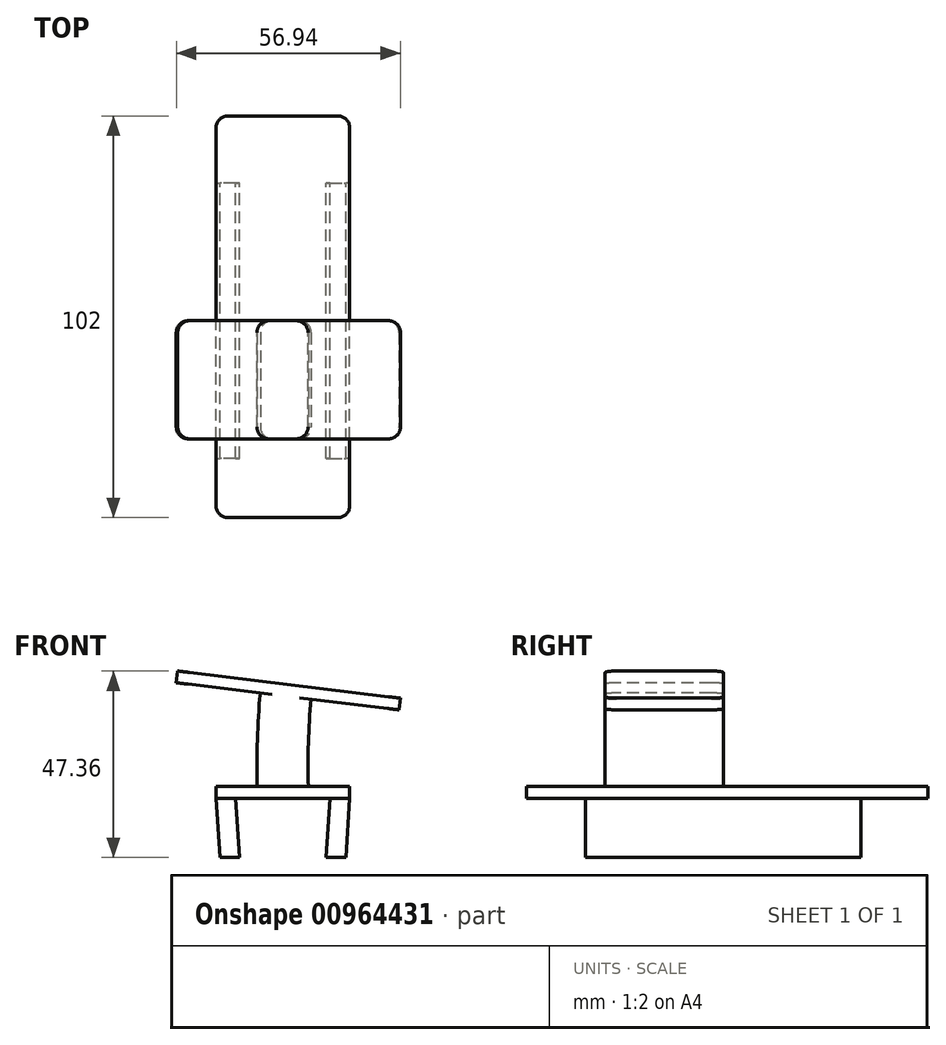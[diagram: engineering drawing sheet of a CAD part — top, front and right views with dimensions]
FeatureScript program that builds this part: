
annotation { "Feature Type Name" : "Feature", "Feature Type Description" : "" }
export const myFeature = defineFeature(function(context is Context, id is Id, definition is map)
    precondition{}
    {
        {
            var Q0;
            Q0=qCreatedBy(makeId("Top.planeOp"),FACE);
            var sketch = newSketch(context, id + "F0", { "sketchPlane" : qUnion([Q0])});
            skLineSegment(sketch, "E0.bottom", {"start": v(-17, -50) * mm, "end": v(17, -50) * mm});
            skLineSegment(sketch, "E0.top", {"start": v(-17, 52) * mm, "end": v(17, 52) * mm});
            skLineSegment(sketch, "E0.left", {"start": v(-17, -50) * mm, "end": v(-17, 52) * mm});
            skLineSegment(sketch, "E0.right", {"start": v(17, -50) * mm, "end": v(17, 52) * mm});
            skSolve(sketch);
        }
        {
            var Q0;
            Q0=makeQuery(id+"F0.imprint","IMPRINT",FACE,{"disambiguationData":[TD([[makeQuery(id+"F0.imprint","IMPRINT",EDGE,{"derivedFrom":sQuery(id+"F0.wireOp",EDGE,"E0.bottom")}),1.0]])]});
            extrude(context, id + "F1", {"entities" : qUnion([Q0]), "depth" : 3 * mm, "offsetDistance" : 25 * mm});
        }
        {
            var Q0;
            Q0=makeQuery(id+"F1.opExtrude","CAP_FACE",FACE,{"disambiguationData":[OSD([sQuery(id+"F0.wireOp",EDGE,"E0.bottom"),sQuery(id+"F0.wireOp",EDGE,"E0.top"),sQuery(id+"F0.wireOp",EDGE,"E0.left"),sQuery(id+"F0.wireOp",EDGE,"E0.right")])],"isStart":true});
            var sketch = newSketch(context, id + "F2", { "sketchPlane" : qUnion([Q0])});
            skLineSegment(sketch, "E1.bottom", {"start": v(12, 35) * mm, "end": v(17, 35) * mm});
            skLineSegment(sketch, "E1.top", {"start": v(12, -35) * mm, "end": v(17, -35) * mm});
            skLineSegment(sketch, "E1.left", {"start": v(12, 35) * mm, "end": v(12, -35) * mm});
            skLineSegment(sketch, "E1.right", {"start": v(17, 35) * mm, "end": v(17, -35) * mm});
            skLineSegment(sketch, "E2.MirrorCS", {"start": v(-12, 35) * mm, "end": v(-17, 35) * mm});
            skLineSegment(sketch, "E3.MirrorCS", {"start": v(-12, 35) * mm, "end": v(-12, -35) * mm});
            skLineSegment(sketch, "E4.MirrorCS", {"start": v(-17, 35) * mm, "end": v(-17, -35) * mm});
            skLineSegment(sketch, "E5.MirrorCS", {"start": v(-12, -35) * mm, "end": v(-17, -35) * mm});
            skSolve(sketch);
        }
        {
            var Q0;
            Q0=makeQuery(id+"F1.opExtrude","CAP_FACE",FACE,{"disambiguationData":[OSD([sQuery(id+"F0.wireOp",EDGE,"E0.bottom"),sQuery(id+"F0.wireOp",EDGE,"E0.top"),sQuery(id+"F0.wireOp",EDGE,"E0.left"),sQuery(id+"F0.wireOp",EDGE,"E0.right")])],"isStart":false});
            var sketch = newSketch(context, id + "F3", { "sketchPlane" : qUnion([Q0])});
            skLineSegment(sketch, "E6", {"start": v(0, 0) * mm, "end": v(-6.5, 0) * mm});
            skLineSegment(sketch, "E7", {"start": v(-6.5, 0) * mm, "end": v(-6.5, -30) * mm});
            skLineSegment(sketch, "E8", {"start": v(-6.5, -30) * mm, "end": v(0, -30) * mm});
            skLineSegment(sketch, "E9.MirrorCS", {"start": v(0, 0) * mm, "end": v(6.5, 0) * mm});
            skLineSegment(sketch, "E10.MirrorCS", {"start": v(6.5, 0) * mm, "end": v(6.5, -30) * mm});
            skLineSegment(sketch, "E11.MirrorCS", {"start": v(6.5, -30) * mm, "end": v(0, -30) * mm});
            skSolve(sketch);
        }
        {
            var Q0;
            Q0=qCreatedBy(makeId("Front.planeOp"),FACE);
            var sketch = newSketch(context, id + "F4", { "sketchPlane" : qUnion([Q0])});
            skArc(sketch, "E12", {"start": v(0.73, 26) * mm, "mid": v(0.02, 14.51) * mm, "end": v(0, 3) * mm});
            skSolve(sketch);
        }
        {
            var Q0;
            Q0=makeQuery(id+"F3.imprint","IMPRINT",FACE,{"disambiguationData":[TD([[makeQuery(id+"F3.imprint","IMPRINT",EDGE,{"derivedFrom":sQuery(id+"F3.wireOp",EDGE,"E6")}),1.0]])]});
            var Q1;
            Q1=sQuery(id+"F4.wireOp",EDGE,"E12");
            sweep(context, id + "F5", {"operationType" : NewBodyOperationType.ADD, "profiles" : qUnion([Q0]), "path" : qUnion([Q1])});
        }
        {
            var Q0;
            Q0=makeQuery(id+"F5.opSweep","CAP_FACE",FACE,{"disambiguationData":[OSD([sQuery(id+"F3.wireOp",EDGE,"E6"),sQuery(id+"F3.wireOp",EDGE,"E7"),sQuery(id+"F3.wireOp",EDGE,"E8"),sQuery(id+"F3.wireOp",EDGE,"E9.MirrorCS"),sQuery(id+"F3.wireOp",EDGE,"E10.MirrorCS"),sQuery(id+"F3.wireOp",EDGE,"E11.MirrorCS"),sQuery(id+"F4.wireOp",VERTEX,"869nxc77-Ht1Q-01pG-Etso-BT9mhs7BUcH0.start")])],"isStart":false});
            var sketch = newSketch(context, id + "F6", { "sketchPlane" : qUnion([Q0])});
            skLineSegment(sketch, "E13.bottom", {"start": v(-30.42, 0) * mm, "end": v(26.58, 0) * mm});
            skLineSegment(sketch, "E13.top", {"start": v(-30.42, -30) * mm, "end": v(26.58, -30) * mm});
            skLineSegment(sketch, "E13.left", {"start": v(-30.42, 0) * mm, "end": v(-30.42, -30) * mm});
            skLineSegment(sketch, "E13.right", {"start": v(26.58, 0) * mm, "end": v(26.58, -30) * mm});
            skSolve(sketch);
        }
        {
            var Q0;
            {var subQ2=sQuery(id+"F6.wireOp",EDGE,"E13.left");Q0=makeQuery(id+"F6.imprint","IMPRINT",FACE,{"disambiguationData":[TD([[makeQuery(id+"F6.imprint","IMPRINT",EDGE,{"derivedFrom":subQ2}),1.0]])]});}
            var Q1;
            {var subQ2=sQuery(id+"F6.wireOp",EDGE,"E13.right");Q1=makeQuery(id+"F6.imprint","IMPRINT",FACE,{"disambiguationData":[TD([[makeQuery(id+"F6.imprint","IMPRINT",EDGE,{"derivedFrom":subQ2}),-1.0]])]});}
            var Q2;
            {var subQ1=sQuery(id+"F4.wireOp",VERTEX,"869nxc77-Ht1Q-01pG-Etso-BT9mhs7BUcH0.start");var subQ2=makeQuery(id+"F5.opSweep","CAP_EDGE",EDGE,{"disambiguationData":[OSD([sQuery(id+"F3.wireOp",EDGE,"E7"),subQ1])],"isStart":false});Q2=makeQuery(id+"F6.imprint","IMPRINT",FACE,{"disambiguationData":[TD([[makeQuery(id+"F6.imprint","IMPRINT",EDGE,{"derivedFrom":subQ2}),1.0]])]});}
            extrude(context, id + "F7", {"entities" : qUnion([Q0, Q1, Q2]), "operationType" : NewBodyOperationType.ADD, "depth" : 3 * mm, "offsetDistance" : 25 * mm});
        }
        {
            var Q0;
            Q0=makeQuery(id+"F7.opExtrude","SWEPT_EDGE",EDGE,{"disambiguationData":[OSD([sQuery(id+"F6.wireOp",EDGE,"E13.top"),sQuery(id+"F6.wireOp",EDGE,"E13.right")])]});
            var Q1;
            Q1=makeQuery(id+"F7.opExtrude","SWEPT_EDGE",EDGE,{"disambiguationData":[OSD([sQuery(id+"F6.wireOp",EDGE,"E13.bottom"),sQuery(id+"F6.wireOp",EDGE,"E13.right")])]});
            var Q2;
            Q2=makeQuery(id+"F7.opExtrude","SWEPT_EDGE",EDGE,{"disambiguationData":[OSD([sQuery(id+"F6.wireOp",EDGE,"E13.top"),sQuery(id+"F6.wireOp",EDGE,"E13.left")])]});
            var Q3;
            Q3=makeQuery(id+"F7.opExtrude","SWEPT_EDGE",EDGE,{"disambiguationData":[OSD([sQuery(id+"F6.wireOp",EDGE,"E13.bottom"),sQuery(id+"F6.wireOp",EDGE,"E13.left")])]});
            fillet(context, id + "F8", {"entities" : qUnion([Q0, Q1, Q2, Q3]), "radius" : 3 * mm, "tangentPropagation" : true, "allowEdgeOverflow" : false});
        }
        {
            var Q0;
            Q0=qCreatedBy(makeId("Top.planeOp"),FACE);
            cPlane(context, id + "F9", {"entities" : qUnion([Q0]), "cplaneType" : CPlaneType.OFFSET, "offset" : 15 * mm, "oppositeDirection" : true, "width" : 150 * mm, "height" : 150 * mm});
        }
        {
            var Q0;
            Q0=qCreatedBy(id+"F9.planeOp",FACE);
            var sketch = newSketch(context, id + "F10", { "sketchPlane" : qUnion([Q0])});
            skLineSegment(sketch, "E14.bottom", {"start": v(11, -35) * mm, "end": v(16, -35) * mm});
            skLineSegment(sketch, "E14.top", {"start": v(11, 35) * mm, "end": v(16, 35) * mm});
            skLineSegment(sketch, "E14.left", {"start": v(11, -35) * mm, "end": v(11, 35) * mm});
            skLineSegment(sketch, "E14.right", {"start": v(16, -35) * mm, "end": v(16, 35) * mm});
            skLineSegment(sketch, "E15.MirrorCS", {"start": v(-11, -35) * mm, "end": v(-11, 35) * mm});
            skLineSegment(sketch, "E16.MirrorCS", {"start": v(-11, -35) * mm, "end": v(-16, -35) * mm});
            skLineSegment(sketch, "E17.MirrorCS", {"start": v(-16, -35) * mm, "end": v(-16, 35) * mm});
            skLineSegment(sketch, "E18.MirrorCS", {"start": v(-11, 35) * mm, "end": v(-16, 35) * mm});
            skSolve(sketch);
        }
        {
            var Q1;
            Q1=makeQuery(id+"F2.imprint","IMPRINT",FACE,{"disambiguationData":[TD([[makeQuery(id+"F2.imprint","IMPRINT",EDGE,{"derivedFrom":sQuery(id+"F2.wireOp",EDGE,"E1.bottom")}),-1.0]])]});
            var Q2;
            Q2=makeQuery(id+"F10.imprint","IMPRINT",FACE,{"disambiguationData":[TD([[makeQuery(id+"F10.imprint","IMPRINT",EDGE,{"derivedFrom":sQuery(id+"F10.wireOp",EDGE,"E14.bottom")}),1.0]])]});
            loft(context, id + "F11", {"operationType" : NewBodyOperationType.ADD, "sheetProfilesArray" : [{ "sheetProfileEntities" : qUnion([Q1]) }, { "sheetProfileEntities" : qUnion([Q2]) }]});
        }
        {
            var Q1;
            Q1=makeQuery(id+"F2.imprint","IMPRINT",FACE,{"disambiguationData":[TD([[makeQuery(id+"F2.imprint","IMPRINT",EDGE,{"derivedFrom":sQuery(id+"F2.wireOp",EDGE,"E2.MirrorCS")}),1.0]])]});
            var Q2;
            Q2=makeQuery(id+"F10.imprint","IMPRINT",FACE,{"disambiguationData":[TD([[makeQuery(id+"F10.imprint","IMPRINT",EDGE,{"derivedFrom":sQuery(id+"F10.wireOp",EDGE,"E15.MirrorCS")}),1.0]])]});
            loft(context, id + "F12", {"operationType" : NewBodyOperationType.ADD, "sheetProfilesArray" : [{ "sheetProfileEntities" : qUnion([Q1]) }, { "sheetProfileEntities" : qUnion([Q2]) }]});
        }
        {
            var Q0;
            Q0=makeQuery(id+"F1.opExtrude","SWEPT_EDGE",EDGE,{"disambiguationData":[OSD([sQuery(id+"F0.wireOp",EDGE,"E0.bottom"),sQuery(id+"F0.wireOp",EDGE,"E0.right")])]});
            var Q1;
            Q1=makeQuery(id+"F1.opExtrude","SWEPT_EDGE",EDGE,{"disambiguationData":[OSD([sQuery(id+"F0.wireOp",EDGE,"E0.bottom"),sQuery(id+"F0.wireOp",EDGE,"E0.left")])]});
            var Q2;
            Q2=makeQuery(id+"F1.opExtrude","SWEPT_EDGE",EDGE,{"disambiguationData":[OSD([sQuery(id+"F0.wireOp",EDGE,"E0.top"),sQuery(id+"F0.wireOp",EDGE,"E0.right")])]});
            var Q3;
            Q3=makeQuery(id+"F1.opExtrude","SWEPT_EDGE",EDGE,{"disambiguationData":[OSD([sQuery(id+"F0.wireOp",EDGE,"E0.top"),sQuery(id+"F0.wireOp",EDGE,"E0.left")])]});
            var Q4;
            Q4=makeQuery(id+"F5.opSweep","SWEPT_EDGE",EDGE,{"disambiguationData":[OSD([sQuery(id+"F3.wireOp",EDGE,"E10.MirrorCS"),sQuery(id+"F3.wireOp",EDGE,"E11.MirrorCS"),sQuery(id+"F4.wireOp",EDGE,"E12")])]});
            var Q5;
            Q5=makeQuery(id+"F5.opSweep","SWEPT_EDGE",EDGE,{"disambiguationData":[OSD([sQuery(id+"F3.wireOp",EDGE,"E7"),sQuery(id+"F3.wireOp",EDGE,"E8"),sQuery(id+"F4.wireOp",EDGE,"E12")])]});
            var Q6;
            Q6=makeQuery(id+"F5.opSweep","SWEPT_EDGE",EDGE,{"disambiguationData":[OSD([sQuery(id+"F3.wireOp",EDGE,"E9.MirrorCS"),sQuery(id+"F3.wireOp",EDGE,"E10.MirrorCS"),sQuery(id+"F4.wireOp",EDGE,"E12")])]});
            var Q7;
            Q7=makeQuery(id+"F5.opSweep","SWEPT_EDGE",EDGE,{"disambiguationData":[OSD([sQuery(id+"F3.wireOp",EDGE,"E6"),sQuery(id+"F3.wireOp",EDGE,"E7"),sQuery(id+"F4.wireOp",EDGE,"E12")])]});
            fillet(context, id + "F13", {"entities" : qUnion([Q0, Q1, Q2, Q3, Q4, Q5, Q6, Q7]), "radius" : 3 * mm, "tangentPropagation" : true, "allowEdgeOverflow" : false});
        }
    });
